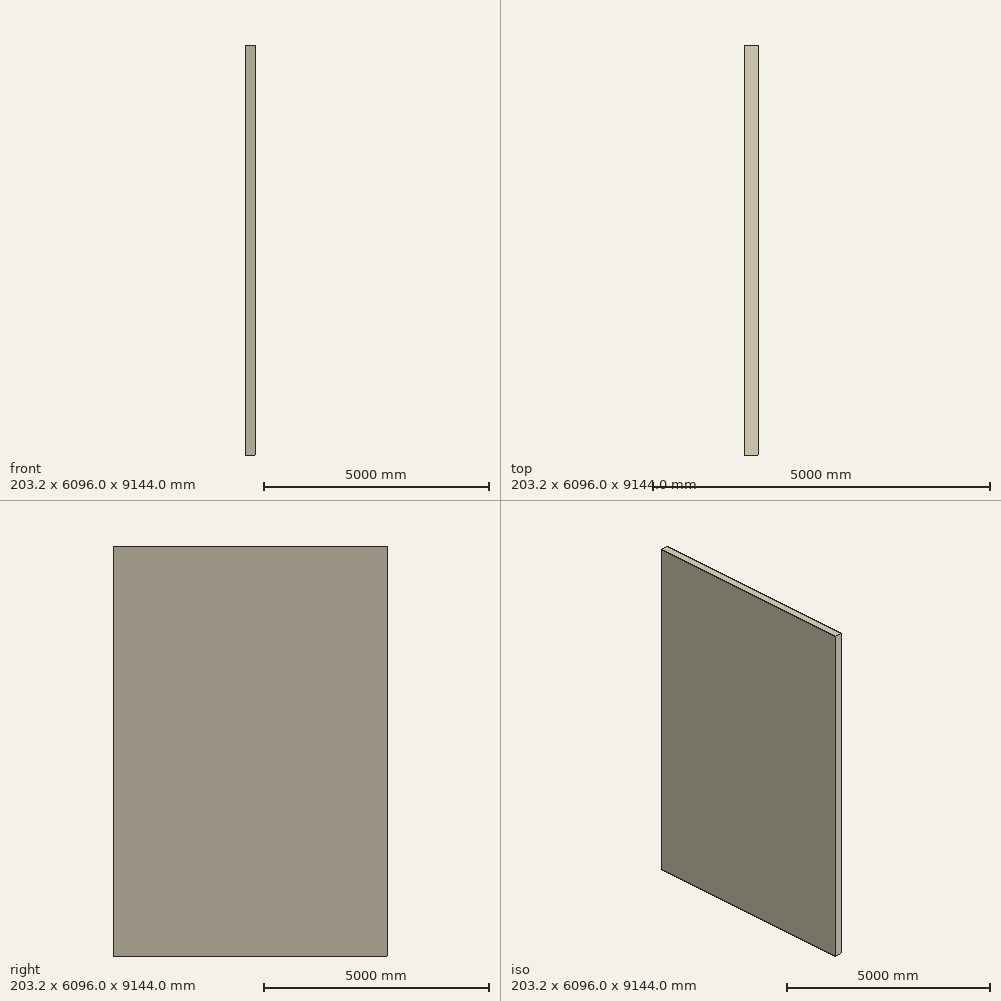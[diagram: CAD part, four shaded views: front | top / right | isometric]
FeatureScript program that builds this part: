
annotation { "Feature Type Name" : "Feature", "Feature Type Description" : "" }
export const myFeature = defineFeature(function(context is Context, id is Id, definition is map)
    precondition{}
    {
        {
            var Q0;
            Q0=qCreatedBy(makeId("Top.planeOp"),FACE);
            var sketch = newSketch(context, id + "F0", { "sketchPlane" : qUnion([Q0])});
            skLineSegment(sketch, "E0.bottom", {"start": v(101.6, 3048) * mm, "end": v(-101.6, 3048) * mm});
            skLineSegment(sketch, "E0.top", {"start": v(101.6, -3048) * mm, "end": v(-101.6, -3048) * mm});
            skLineSegment(sketch, "E0.left", {"start": v(101.6, 3048) * mm, "end": v(101.6, -3048) * mm});
            skLineSegment(sketch, "E0.right", {"start": v(-101.6, 3048) * mm, "end": v(-101.6, -3048) * mm});
            skPoint(sketch, "E0.middle", {"position": v(0, 0) * mm});
            skSolve(sketch);
        }
        {
            var Q0;
            Q0=qSketchRegion(id+"F0",true);
            extrude(context, id + "F1", {"entities" : qUnion([Q0]), "endBound" : BoundingType.SYMMETRIC, "depth" : 9144 * mm});
        }
    });
